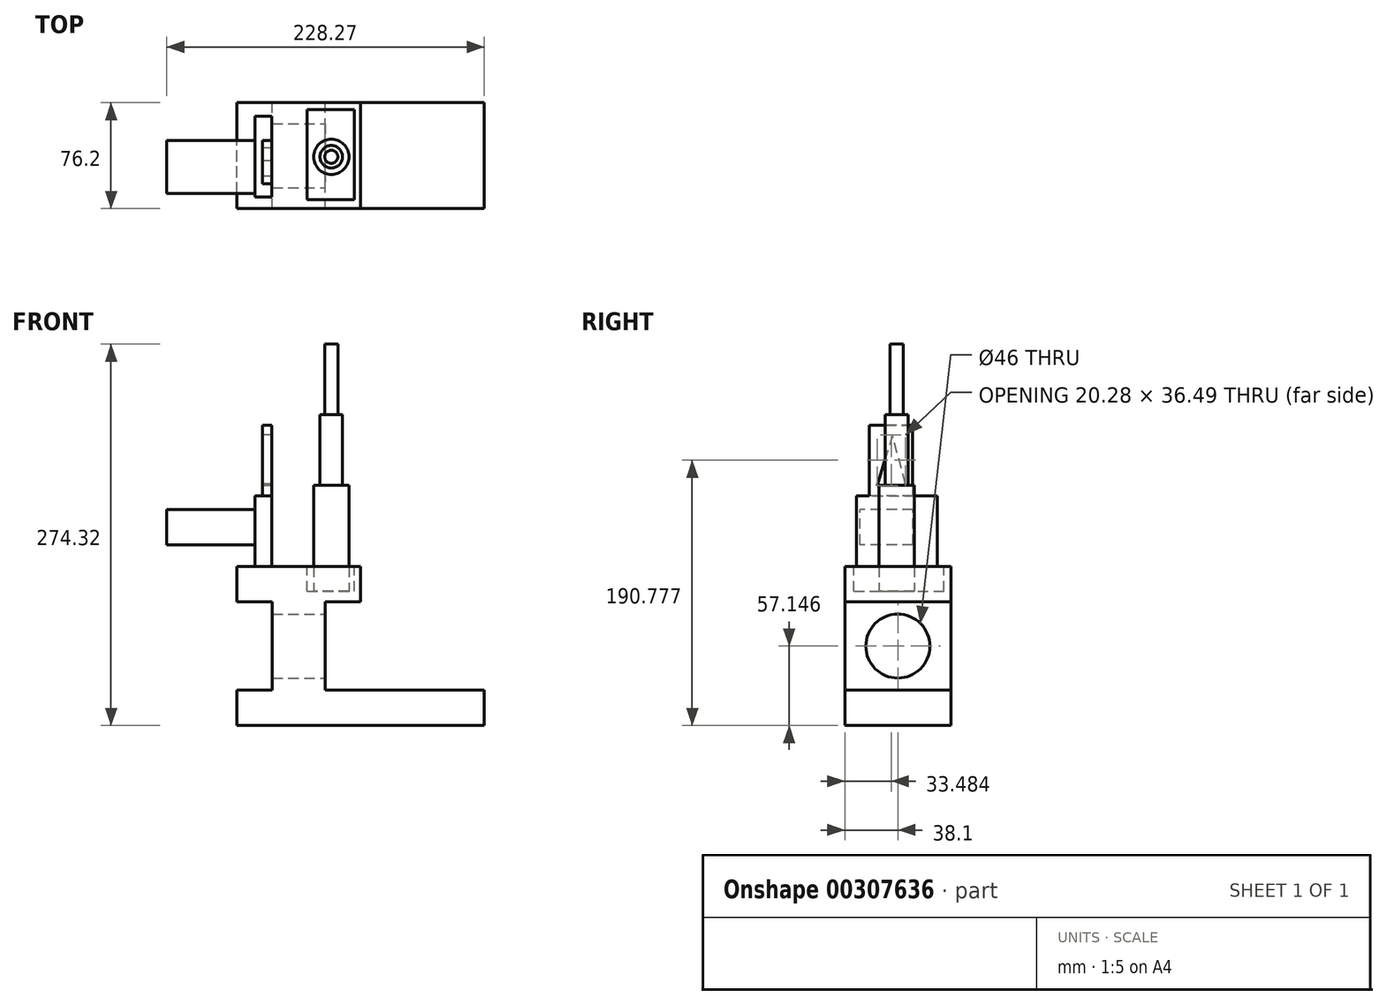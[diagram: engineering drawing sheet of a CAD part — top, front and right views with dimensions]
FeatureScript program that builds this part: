
annotation { "Feature Type Name" : "Feature", "Feature Type Description" : "" }
export const myFeature = defineFeature(function(context is Context, id is Id, definition is map)
    precondition{}
    {
        {
            var Q0;
            Q0=qCreatedBy(makeId("Front.planeOp"),FACE);
            var sketch = newSketch(context, id + "F0", { "sketchPlane" : qUnion([Q0])});
            skLineSegment(sketch, "E0", {"start": v(-45.55, -37.8) * mm, "end": v(43.35, -37.8) * mm});
            skLineSegment(sketch, "E1", {"start": v(43.35, -37.8) * mm, "end": v(43.35, -12.4) * mm});
            skLineSegment(sketch, "E2", {"start": v(43.35, -12.4) * mm, "end": v(17.95, -12.4) * mm});
            skLineSegment(sketch, "E3", {"start": v(17.95, -12.4) * mm, "end": v(17.95, 51.1) * mm});
            skLineSegment(sketch, "E4", {"start": v(17.95, 51.1) * mm, "end": v(43.35, 51.1) * mm});
            skLineSegment(sketch, "E5", {"start": v(43.35, 51.1) * mm, "end": v(43.35, 76.5) * mm});
            skLineSegment(sketch, "E6", {"start": v(43.35, 76.5) * mm, "end": v(-45.55, 76.5) * mm});
            skLineSegment(sketch, "E7", {"start": v(-45.55, 76.5) * mm, "end": v(-45.55, 51.1) * mm});
            skLineSegment(sketch, "E8", {"start": v(-45.55, 51.1) * mm, "end": v(-20.15, 51.1) * mm});
            skLineSegment(sketch, "E9", {"start": v(-20.15, 51.1) * mm, "end": v(-20.15, -12.4) * mm});
            skLineSegment(sketch, "E10", {"start": v(-20.15, -12.4) * mm, "end": v(-45.55, -12.4) * mm});
            skLineSegment(sketch, "E11", {"start": v(-45.55, -12.4) * mm, "end": v(-45.55, -37.8) * mm});
            skSolve(sketch);
        }
        {
            var Q0;
            Q0=makeQuery(id+"F0.imprint","IMPRINT",FACE,{"disambiguationData":[TD([[makeQuery(id+"F0.imprint","IMPRINT",EDGE,{"derivedFrom":sQuery(id+"F0.wireOp",EDGE,"E0")}),1.0]])]});
            extrude(context, id + "F1", {"entities" : qUnion([Q0]), "depth" : 76.2 * mm});
        }
        {
            var Q0;
            Q0=makeQuery(id+"F1.opExtrude","SWEPT_FACE",FACE,{"disambiguationData":[OSD([sQuery(id+"F0.wireOp",EDGE,"E3")])]});
            var sketch = newSketch(context, id + "F2", { "sketchPlane" : qUnion([Q0])});
            skPoint(sketch, "E12.centerSnap0", {"position": v(-38.1, 51.1) * mm});
            skPoint(sketch, "E12.centerSnap1", {"position": v(-76.2, 19.36) * mm});
            skCircle(sketch, "E13", {"center": v(-38.1, 19.36) * mm, "radius": 23 * mm});
            skSolve(sketch);
        }
        {
            var Q0;
            Q0=makeQuery(id+"F2.imprint","IMPRINT",FACE,{"disambiguationData":[TD([[makeQuery(id+"F2.imprint","IMPRINT",EDGE,{"derivedFrom":sQuery(id+"F2.wireOp",EDGE,"E13")}),1.0]])]});
            extrude(context, id + "F3", {"entities" : qUnion([Q0]), "operationType" : NewBodyOperationType.REMOVE, "endBound" : BoundingType.THROUGH_ALL, "oppositeDirection" : true, "depth" : 25.4 * mm});
        }
        {
            var Q0;
            Q0=makeQuery(id+"F1.opExtrude","SWEPT_FACE",FACE,{"disambiguationData":[OSD([sQuery(id+"F0.wireOp",EDGE,"E6")])]});
            var sketch = newSketch(context, id + "F4", { "sketchPlane" : qUnion([Q0])});
            skLineSegment(sketch, "E14.bottom", {"start": v(-32.52, -67.74) * mm, "end": v(-20.54, -67.74) * mm});
            skLineSegment(sketch, "E14.top", {"start": v(-32.52, -9.84) * mm, "end": v(-20.54, -9.84) * mm});
            skLineSegment(sketch, "E14.left", {"start": v(-32.52, -67.74) * mm, "end": v(-32.52, -9.84) * mm});
            skLineSegment(sketch, "E14.right", {"start": v(-20.54, -67.74) * mm, "end": v(-20.54, -9.84) * mm});
            skSolve(sketch);
        }
        {
            var Q0;
            Q0=makeQuery(id+"F4.imprint","IMPRINT",FACE,{"disambiguationData":[TD([[makeQuery(id+"F4.imprint","IMPRINT",EDGE,{"derivedFrom":sQuery(id+"F4.wireOp",EDGE,"E14.bottom")}),1.0]])]});
            extrude(context, id + "F5", {"entities" : qUnion([Q0]), "operationType" : NewBodyOperationType.ADD, "depth" : 50.8 * mm});
        }
        {
            var Q0;
            Q0=makeQuery(id+"F1.opExtrude","SWEPT_FACE",FACE,{"disambiguationData":[OSD([sQuery(id+"F0.wireOp",EDGE,"E6")])]});
            var sketch = newSketch(context, id + "F6", { "sketchPlane" : qUnion([Q0])});
            skLineSegment(sketch, "E15.bottom", {"start": v(4.85, -69.74) * mm, "end": v(38.8, -69.74) * mm});
            skLineSegment(sketch, "E15.top", {"start": v(4.85, -5) * mm, "end": v(38.8, -5) * mm});
            skLineSegment(sketch, "E15.left", {"start": v(4.85, -69.74) * mm, "end": v(4.85, -5) * mm});
            skLineSegment(sketch, "E15.right", {"start": v(38.8, -69.74) * mm, "end": v(38.8, -5) * mm});
            skSolve(sketch);
        }
        {
            var Q0;
            Q0=makeQuery(id+"F6.imprint","IMPRINT",FACE,{"disambiguationData":[TD([[makeQuery(id+"F6.imprint","IMPRINT",EDGE,{"derivedFrom":sQuery(id+"F6.wireOp",EDGE,"E15.bottom")}),1.0]])]});
            extrude(context, id + "F7", {"entities" : qUnion([Q0]), "operationType" : NewBodyOperationType.REMOVE, "oppositeDirection" : true, "depth" : 17.78 * mm});
        }
        {
            var Q0;
            Q0=makeQuery(id+"F7.boolean.opBoolean","COPY",FACE,{"derivedFrom":makeQuery(id+"F7.opExtrude","CAP_FACE",FACE,{"disambiguationData":[OSD([sQuery(id+"F6.wireOp",EDGE,"E15.bottom"),sQuery(id+"F6.wireOp",EDGE,"E15.top"),sQuery(id+"F6.wireOp",EDGE,"E15.left"),sQuery(id+"F6.wireOp",EDGE,"E15.right")])],"isStart":false})});
            var sketch = newSketch(context, id + "F8", { "sketchPlane" : qUnion([Q0])});
            skCircle(sketch, "E16", {"center": v(22.25, -38.94) * mm, "radius": 12.7 * mm});
            skSolve(sketch);
        }
        {
            var Q0;
            Q0 = qSketchRegion(id + "F8", true);
            extrude(context, id + "F9", {"entities" : qUnion([Q0]), "operationType" : NewBodyOperationType.ADD, "depth" : 76.2 * mm});
        }
        {
            var Q0;
            Q0=makeQuery(id+"F5.opExtrude","SWEPT_FACE",FACE,{"disambiguationData":[OSD([sQuery(id+"F4.wireOp",EDGE,"E14.left")])]});
            var sketch = newSketch(context, id + "F10", { "sketchPlane" : qUnion([Q0])});
            skLineSegment(sketch, "E17.bottom", {"start": v(27.25, 92.3) * mm, "end": v(65.35, 92.3) * mm});
            skLineSegment(sketch, "E17.top", {"start": v(27.25, 117.7) * mm, "end": v(65.35, 117.7) * mm});
            skLineSegment(sketch, "E17.left", {"start": v(27.25, 92.3) * mm, "end": v(27.25, 117.7) * mm});
            skLineSegment(sketch, "E17.right", {"start": v(65.35, 92.3) * mm, "end": v(65.35, 117.7) * mm});
            skSolve(sketch);
        }
        {
            var Q0;
            Q0=makeQuery(id+"F10.imprint","IMPRINT",FACE,{"disambiguationData":[TD([[makeQuery(id+"F10.imprint","IMPRINT",EDGE,{"derivedFrom":sQuery(id+"F10.wireOp",EDGE,"E17.bottom")}),1.0]])]});
            extrude(context, id + "F11", {"entities" : qUnion([Q0]), "operationType" : NewBodyOperationType.ADD, "depth" : 63.5 * mm});
        }
        {
            var Q0;
            Q0=makeQuery(id+"F9.opExtrude","CAP_FACE",FACE,{"disambiguationData":[OSD([sQuery(id+"F8.wireOp",EDGE,"E16")])],"isStart":false});
            var sketch = newSketch(context, id + "F12", { "sketchPlane" : qUnion([Q0])});
            skCircle(sketch, "E18", {"center": v(22.25, -38.94) * mm, "radius": 8.14 * mm});
            skSolve(sketch);
        }
        {
            var Q0;
            Q0=makeQuery(id+"F12.imprint","IMPRINT",FACE,{"disambiguationData":[TD([[makeQuery(id+"F12.imprint","IMPRINT",EDGE,{"derivedFrom":sQuery(id+"F12.wireOp",EDGE,"E18")}),1.0]])]});
            extrude(context, id + "F13", {"entities" : qUnion([Q0]), "operationType" : NewBodyOperationType.ADD, "depth" : 50.8 * mm});
        }
        {
            var Q0;
            Q0=makeQuery(id+"F13.opExtrude","CAP_FACE",FACE,{"disambiguationData":[OSD([sQuery(id+"F12.wireOp",EDGE,"E18")])],"isStart":false});
            var sketch = newSketch(context, id + "F14", { "sketchPlane" : qUnion([Q0])});
            skCircle(sketch, "E19", {"center": v(22.25, -38.94) * mm, "radius": 4.72 * mm});
            skSolve(sketch);
        }
        {
            var Q0;
            Q0=makeQuery(id+"F14.imprint","IMPRINT",FACE,{"disambiguationData":[TD([[makeQuery(id+"F14.imprint","IMPRINT",EDGE,{"derivedFrom":sQuery(id+"F14.wireOp",EDGE,"E19")}),1.0]])]});
            extrude(context, id + "F15", {"entities" : qUnion([Q0]), "operationType" : NewBodyOperationType.ADD, "depth" : 50.8 * mm});
        }
        {
            var Q0;
            Q0=makeQuery(id+"F5.opExtrude","CAP_FACE",FACE,{"disambiguationData":[OSD([sQuery(id+"F4.wireOp",EDGE,"E14.bottom"),sQuery(id+"F4.wireOp",EDGE,"E14.top"),sQuery(id+"F4.wireOp",EDGE,"E14.left"),sQuery(id+"F4.wireOp",EDGE,"E14.right")])],"isStart":false});
            var sketch = newSketch(context, id + "F16", { "sketchPlane" : qUnion([Q0])});
            skLineSegment(sketch, "E20.bottom", {"start": v(-27.11, -27.34) * mm, "end": v(-20.54, -27.34) * mm});
            skLineSegment(sketch, "E20.top", {"start": v(-27.11, -58.47) * mm, "end": v(-20.54, -58.47) * mm});
            skLineSegment(sketch, "E20.left", {"start": v(-27.11, -27.34) * mm, "end": v(-27.11, -58.47) * mm});
            skLineSegment(sketch, "E20.right", {"start": v(-20.54, -27.34) * mm, "end": v(-20.54, -58.47) * mm});
            skSolve(sketch);
        }
        {
            var Q0;
            Q0=makeQuery(id+"F16.imprint","IMPRINT",FACE,{"disambiguationData":[TD([[makeQuery(id+"F16.imprint","IMPRINT",EDGE,{"derivedFrom":sQuery(id+"F16.wireOp",EDGE,"E20.bottom")}),-1.0]])]});
            extrude(context, id + "F17", {"entities" : qUnion([Q0]), "operationType" : NewBodyOperationType.ADD, "depth" : 50.8 * mm});
        }
        {
            var Q0;
            Q0=makeQuery(id+"F17.opExtrude","SWEPT_FACE",FACE,{"disambiguationData":[OSD([sQuery(id+"F16.wireOp",EDGE,"E20.left")])]});
            var sketch = newSketch(context, id + "F18", { "sketchPlane" : qUnion([Q0])});
            skLineSegment(sketch, "E21", {"start": v(32.57, 135.97) * mm, "end": v(41.9, 171.23) * mm});
            skLineSegment(sketch, "E22", {"start": v(41.9, 171.23) * mm, "end": v(52.86, 134.74) * mm});
            skLineSegment(sketch, "E23", {"start": v(52.86, 134.74) * mm, "end": v(32.57, 135.97) * mm});
            skSolve(sketch);
        }
        {
            var Q0;
            Q0=makeQuery(id+"F18.imprint","IMPRINT",FACE,{"disambiguationData":[TD([[makeQuery(id+"F18.imprint","IMPRINT",EDGE,{"derivedFrom":sQuery(id+"F18.wireOp",EDGE,"E21")}),-1.0]])]});
            extrude(context, id + "F19", {"entities" : qUnion([Q0]), "operationType" : NewBodyOperationType.REMOVE, "oppositeDirection" : true, "depth" : 30.48 * mm});
        }
        {
            var Q0;
            Q0=makeQuery(id+"F1.opExtrude","SWEPT_FACE",FACE,{"disambiguationData":[OSD([sQuery(id+"F0.wireOp",EDGE,"E1")])]});
            var sketch = newSketch(context, id + "F20", { "sketchPlane" : qUnion([Q0])});
            skLineSegment(sketch, "E24", {"start": v(-76.2, -37.8) * mm, "end": v(-76.2, -12.4) * mm});
            skLineSegment(sketch, "E25", {"start": v(-76.2, -12.4) * mm, "end": v(0, -12.4) * mm});
            skLineSegment(sketch, "E26", {"start": v(0, -12.4) * mm, "end": v(0, -37.8) * mm});
            skLineSegment(sketch, "E27", {"start": v(0, -37.8) * mm, "end": v(-76.2, -37.8) * mm});
            skSolve(sketch);
        }
        {
            var Q0;
            Q0=makeQuery(id+"F20.imprint","IMPRINT",FACE,{"disambiguationData":[TD([[makeQuery(id+"F20.imprint","IMPRINT",EDGE,{"derivedFrom":sQuery(id+"F20.wireOp",EDGE,"E24")}),-1.0]])]});
            extrude(context, id + "F21", {"entities" : qUnion([Q0]), "operationType" : NewBodyOperationType.ADD, "depth" : 88.9 * mm});
        }
    });
